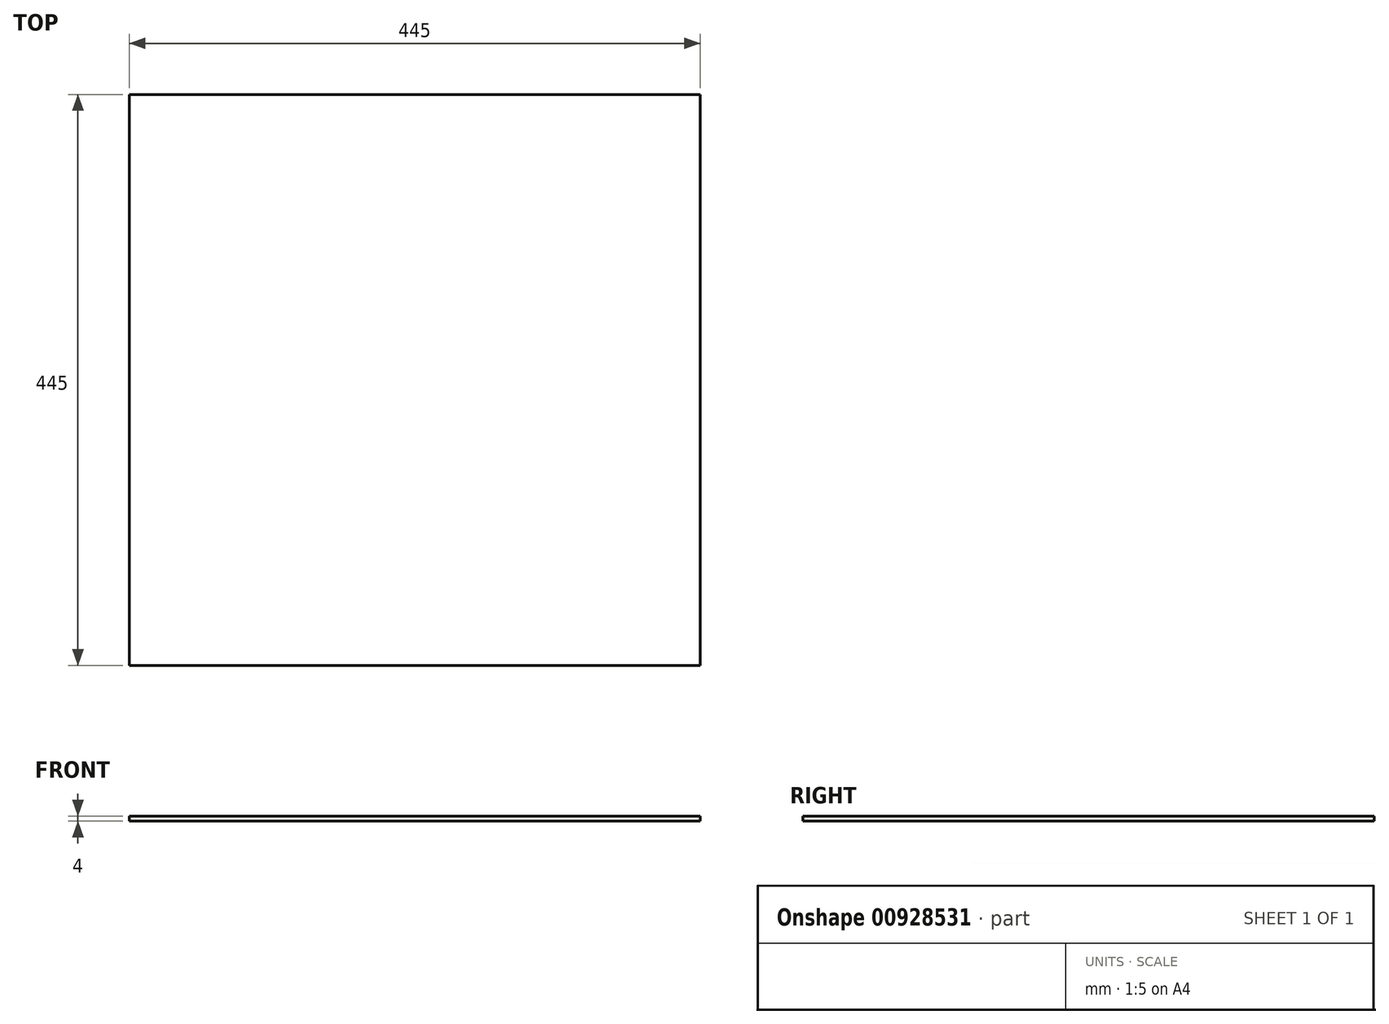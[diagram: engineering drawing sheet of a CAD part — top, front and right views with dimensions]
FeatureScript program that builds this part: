
annotation { "Feature Type Name" : "Feature", "Feature Type Description" : "" }
export const myFeature = defineFeature(function(context is Context, id is Id, definition is map)
    precondition{}
    {
        {
            var Q0;
            Q0=qCreatedBy(makeId("Top.planeOp"),FACE);
            var sketch = newSketch(context, id + "F0", { "sketchPlane" : qUnion([Q0])});
            skLineSegment(sketch, "E0.bottom", {"start": v(-121.47, 0) * mm, "end": v(323.53, 0) * mm});
            skLineSegment(sketch, "E0.top", {"start": v(-121.47, -445) * mm, "end": v(323.53, -445) * mm});
            skLineSegment(sketch, "E0.left", {"start": v(-121.47, 0) * mm, "end": v(-121.47, -445) * mm});
            skLineSegment(sketch, "E0.right", {"start": v(323.53, 0) * mm, "end": v(323.53, -445) * mm});
            skSolve(sketch);
        }
        {
            var Q0;
            Q0 = qSketchRegion(id + "F0", true);
            extrude(context, id + "F1", {"entities" : qUnion([Q0]), "depth" : 4 * mm, "offsetDistance" : 25 * mm});
        }
    });
